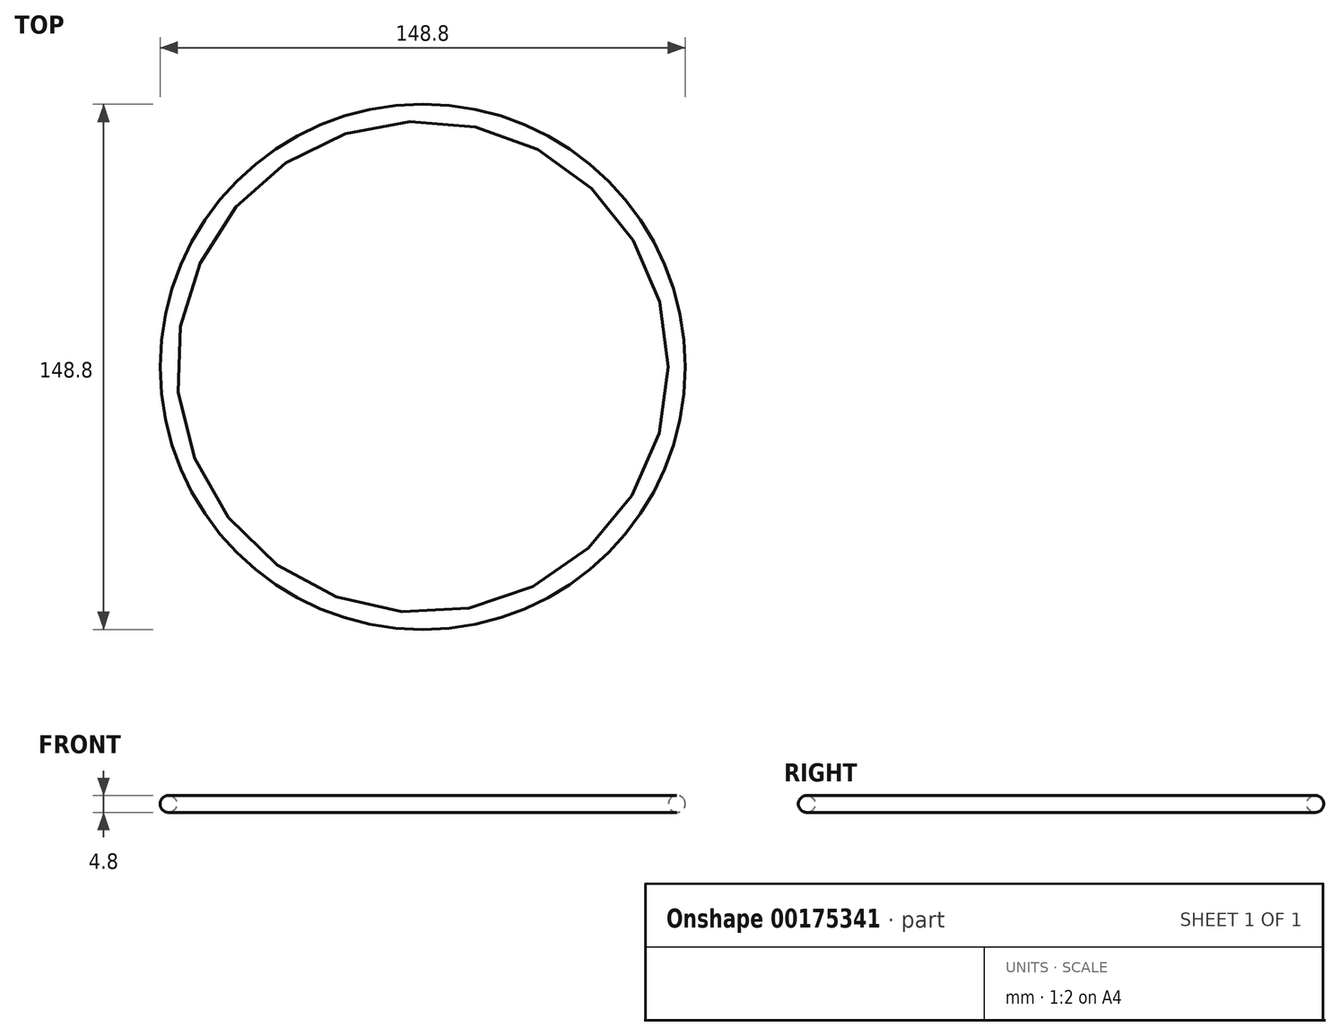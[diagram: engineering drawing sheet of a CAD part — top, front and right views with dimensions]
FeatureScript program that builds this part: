
annotation { "Feature Type Name" : "Feature", "Feature Type Description" : "" }
export const myFeature = defineFeature(function(context is Context, id is Id, definition is map)
    precondition{}
    {
        {
            var Q0;
            Q0=qCreatedBy(makeId("Front.planeOp"),FACE);
            var sketch = newSketch(context, id + "F0", { "sketchPlane" : qUnion([Q0])});
            skCircle(sketch, "E0", {"center": v(0, 0) * mm, "radius": 2.4 * mm});
            skLineSegment(sketch, "E1", {"start": v(72, 12.83) * mm, "end": v(72, -19.42) * mm, "construction": true});
            skSolve(sketch);
        }
        {
            var Q0;
            Q0 = qSketchRegion(id + "F0", true);
            var Q1;
            Q1=sQuery(id+"F0.wireOp",EDGE,"E1");
            revolve(context, id + "F1", {"entities" : qUnion([Q0]), "axis" : qUnion([Q1]), "revolveType" : RevolveType.FULL});
        }
    });
